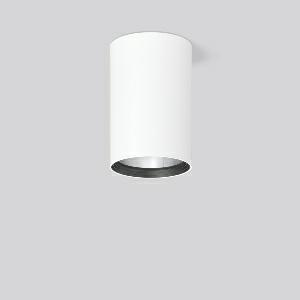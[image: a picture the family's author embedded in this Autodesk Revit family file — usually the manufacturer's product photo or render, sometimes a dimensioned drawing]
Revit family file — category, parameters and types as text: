
# Revit family: heledon_maxi_a_931223_002_2_76_f189
name_source: partatom
category: Lighting Fixtures
units: mm (PartAtom-declared; Revit-internal decimal feet)

## family parameters
Cut with Voids When Loaded = No
Host = Face
Light Source = No
Part Type = Normal
Room Calculation Point = No
Round Connector Dimension = Use Diameter
Shared = No

## types (1)
- HELEDON maxi A (1 x LED Modul 927, 4000 lm, 2700)
    Apparent Load = 35 VA
    Approval mark = CE
    CIE Flux Codes = 100 100 100 100 100
    Color Rendering = 92
    Color Temperature = 2700
    Default Elevation = 1800 mm
    Description = Series: HELEDON maxi
Cylindrical surface-mounted downlight. Housing: die-cast aluminium, powder-coated. Internal ceiling frame polycarbonate with bayonet mounting. Black plastic ring and recessed LED to prevent glare from the side. Optical assembly with reflector made of MIRO-Silver with 98% total light reflection for outstanding efficiency - can be changed without tools. Best colour rendering index Ra>90. Suitable for Ceiling mounting. Easy installation with a separate ceiling frame with bayonet mounting and plug connection. Driver integrated. Connected via plug-in connector. High quality converter without flickering and stroboscopic effect. The following accessories can be mounted without use of tools: interchangeable lenses, decorative glasses, honeycomb louvre, clear and frosted diffusers, white interchangeable plastic ring. 
Colour: traffic white, matt (RAL 9016)
Diameter: 123 mm
Height: 183 mm
Lamp: LED
Socket: without socket
Colour temperature: 2700K
Colour rendering index (CRI): 92
System power: 35 W
Rated luminous flux: 4000 lm
Luminous efficiency: 114 lm/W
Control gear: Converter, dimmable, DALI
Protection class: I
Type of protection: IP 20
    Height = 183 mm
    Lamp = 1 x LED Modul 927
    Lamp Light Flux = 4000 lm
    Lamp count = 1
    Length = 123 mm
    Lifetime = 50000 h
    Luminous efficacy = 114 lm/W
    Manufacturer = RZB
    ModVariant = No
    Model = 931223.002.2.76
    Mounting Place = Ceiling
    Mounting Type = Surface mounted
    Number of Poles = 1
    OnlyDefault = Yes
    Power Factor = 1
    Product Name = HELEDON maxi A
    Product group = Surface mounted downlights
    ProductGroupID = 302
    Protection Class = Protection class I
    Protection Degree = IP 20
    RLX_Detail_Level = 1
    RLX_Emergency_Light_Flux = 0 lm
    RLX_Emergency_Type = 0
    RLX_Emergency_Type_DB = No
    RlxData = <blob elided: 96609 chars, md5=26b24aa6>
    Socket = socket
    Standby Power = 0 W
    System Light Flux = 4000 lm
    System Power = 35 W
    Type Comments = Product without accessories
    Type Image = 931192.002.jpg
    URL = http://relux.com
    VarID = ---
    Voltage = 230 V
    Voltage Range = 220-240 V
    Weight = 0.00 kg
    Width = 0 mm  [stored 0 ft]

note: [stored X ft] marks values corroborated as IEEE doubles in the binary element streams (Revit-internal decimal feet)

## geometry (parser evidence)
native form markers: Blend x4, Sweep x10
no freeform markers — native parametric forms only
